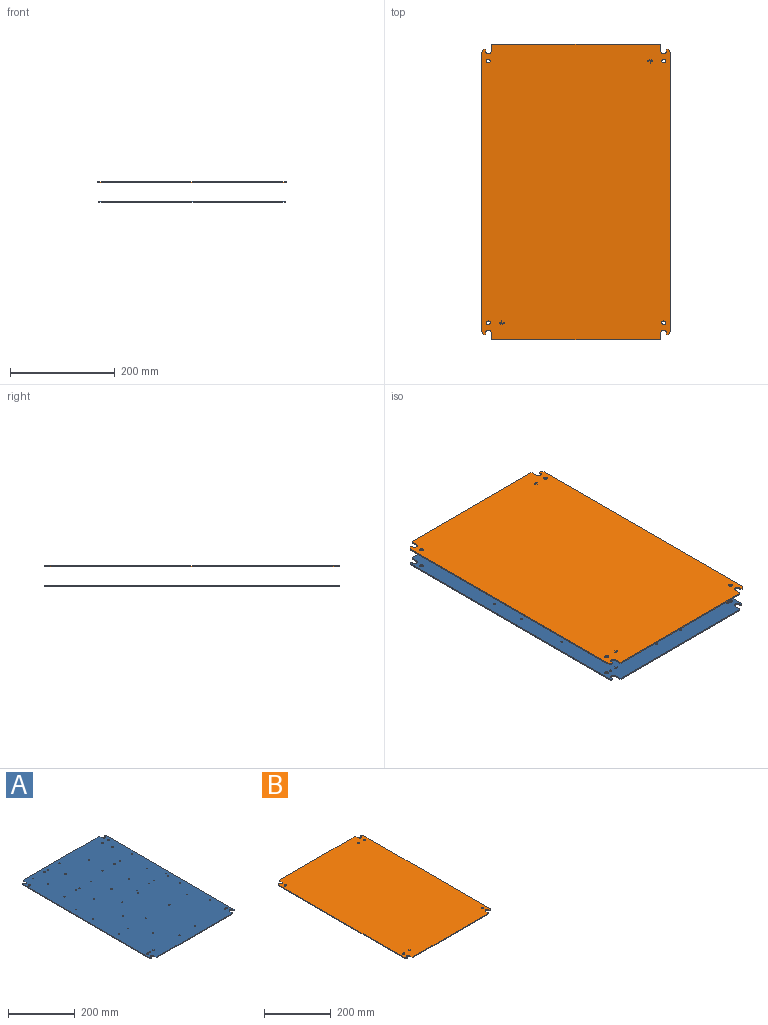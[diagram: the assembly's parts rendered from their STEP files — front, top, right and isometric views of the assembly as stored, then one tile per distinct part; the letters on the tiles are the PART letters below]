
ASSEMBLY  parts=2 mates=1
PART A: 146 faces, bbox 355.3x563.9x2.5 mm
  f0: plane 3.18x0.76mm, normal (0,0,1), area 2.4mm2, adj f6,f7,f8,f9
  f1: plane 9.53x5.13mm, normal (0,0,1), area 10.6mm2, adj f10,f11,f12,f13,f14,f15,f16,f17
  f2: plane 6.35x0.76mm, normal (0,0,1), area 4.8mm2, adj f18,f19,f20,f21
  f3: plane 3.18x0.76mm, normal (0,0,1), area 2.4mm2, adj f22,f23,f24,f25
  f4: plane 6.35x0.76mm, normal (0,0,1), area 4.8mm2, adj f26,f27,f28,f29
  f5: plane 9.53x5.13mm, normal (0,0,1), area 10.6mm2, adj f30,f31,f32,f33,f34,f35,f36,f37
  f6: plane 0.76x0.71mm, normal (1,0,0), area 0.5mm2, adj f0,f7,f9,f38
  f7: plane 3.18x0.71mm, normal (0,-1,0), area 2.3mm2, adj f0,f6,f8,f39
  f8: plane 0.76x0.71mm, normal (-1,0,0), area 0.5mm2, adj f0,f7,f9,f40
  f9: plane 3.18x0.71mm, normal (0,1,0), area 2.3mm2, adj f0,f6,f8,f41
  f10: plane 4.37x0.71mm, normal (1,0,0), area 3.1mm2, adj f1,f11,f17,f42
  f11: plane 0.76x0.71mm, normal (0,-1,0), area 0.5mm2, adj f1,f10,f12,f43
  f12: plane 4.37x0.71mm, normal (-1,0,0), area 3.1mm2, adj f1,f11,f13,f44
  f13: plane 4.38x0.71mm, normal (0,-1,0), area 3.1mm2, adj f1,f12,f14,f45
  f14: plane 0.76x0.71mm, normal (-1,0,0), area 0.5mm2, adj f1,f13,f15,f46
  f15: plane 9.53x0.71mm, normal (0,1,0), area 6.8mm2, adj f1,f14,f16,f47
  f16: plane 0.76x0.71mm, normal (1,0,0), area 0.5mm2, adj f1,f15,f17,f48
  f17: plane 4.38x0.71mm, normal (0,-1,0), area 3.1mm2, adj f1,f10,f16,f49
  f18: plane 0.76x0.71mm, normal (-1,0,0), area 0.5mm2, adj f2,f19,f21,f50
  f19: plane 6.35x0.71mm, normal (0,1,0), area 4.5mm2, adj f2,f18,f20,f51
  f20: plane 0.76x0.71mm, normal (1,0,0), area 0.5mm2, adj f2,f19,f21,f52
  f21: plane 6.35x0.71mm, normal (0,-1,0), area 4.5mm2, adj f2,f18,f20,f53
  f22: plane 0.76x0.71mm, normal (-1,0,0), area 0.5mm2, adj f3,f23,f25,f54
  f23: plane 3.18x0.71mm, normal (0,1,0), area 2.3mm2, adj f3,f22,f24,f55
  f24: plane 0.76x0.71mm, normal (1,0,0), area 0.5mm2, adj f3,f23,f25,f56
  f25: plane 3.18x0.71mm, normal (0,-1,0), area 2.3mm2, adj f3,f22,f24,f57
  f26: plane 0.76x0.71mm, normal (1,0,0), area 0.5mm2, adj f4,f27,f29,f58
  f27: plane 6.35x0.71mm, normal (0,-1,0), area 4.5mm2, adj f4,f26,f28,f59
  f28: plane 0.76x0.71mm, normal (-1,0,0), area 0.5mm2, adj f4,f27,f29,f60
  f29: plane 6.35x0.71mm, normal (0,1,0), area 4.5mm2, adj f4,f26,f28,f61
  f30: plane 4.37x0.71mm, normal (-1,0,0), area 3.1mm2, adj f5,f31,f37,f62
  f31: plane 0.76x0.71mm, normal (0,1,0), area 0.5mm2, adj f5,f30,f32,f63
  f32: plane 4.37x0.71mm, normal (1,0,0), area 3.1mm2, adj f5,f31,f33,f64
  f33: plane 4.38x0.71mm, normal (0,1,0), area 3.1mm2, adj f5,f32,f34,f65
  f34: plane 0.76x0.71mm, normal (1,0,0), area 0.5mm2, adj f5,f33,f35,f66
  f35: plane 9.53x0.71mm, normal (0,-1,0), area 6.8mm2, adj f5,f34,f36,f67
  f36: plane 0.76x0.71mm, normal (-1,0,0), area 0.5mm2, adj f5,f35,f37,f68
  f37: plane 4.38x0.71mm, normal (0,1,0), area 3.1mm2, adj f5,f30,f36,f69
  f38: plane 0.86x0.05mm, normal (0.71,0,0.71), area 0.1mm2, adj f6,f39,f41,f70
  f39: plane 3.28x0.05mm, normal (0,-0.71,0.71), area 0.2mm2, adj f7,f38,f40,f70
  f40: plane 0.86x0.05mm, normal (-0.71,0,0.71), area 0.1mm2, adj f8,f39,f41,f70
  f41: plane 3.28x0.05mm, normal (0,0.71,0.71), area 0.2mm2, adj f9,f38,f40,f70
  f42: plane 4.42x0.05mm, normal (0.71,0,0.71), area 0.3mm2, adj f10,f43,f49,f70
  f43: plane 0.86x0.05mm, normal (0,-0.71,0.71), area 0.1mm2, adj f11,f42,f44,f70
  f44: plane 4.42x0.05mm, normal (-0.71,0,0.71), area 0.3mm2, adj f12,f43,f45,f70
  f45: plane 4.43x0.05mm, normal (0,-0.71,0.71), area 0.3mm2, adj f13,f44,f46,f70
  f46: plane 0.86x0.05mm, normal (-0.71,0,0.71), area 0.1mm2, adj f14,f45,f47,f70
  f47: plane 9.63x0.05mm, normal (0,0.71,0.71), area 0.7mm2, adj f15,f46,f48,f70
  f48: plane 0.86x0.05mm, normal (0.71,0,0.71), area 0.1mm2, adj f16,f47,f49,f70
  f49: plane 4.43x0.05mm, normal (0,-0.71,0.71), area 0.3mm2, adj f17,f42,f48,f70
  f50: plane 0.86x0.05mm, normal (-0.71,0,0.71), area 0.1mm2, adj f18,f51,f53,f70
  f51: plane 6.45x0.05mm, normal (0,0.71,0.71), area 0.5mm2, adj f19,f50,f52,f70
  f52: plane 0.86x0.05mm, normal (0.71,0,0.71), area 0.1mm2, adj f20,f51,f53,f70
  f53: plane 6.45x0.05mm, normal (0,-0.71,0.71), area 0.5mm2, adj f21,f50,f52,f70
  f54: plane 0.86x0.05mm, normal (-0.71,0,0.71), area 0.1mm2, adj f22,f55,f57,f70
  f55: plane 3.28x0.05mm, normal (0,0.71,0.71), area 0.2mm2, adj f23,f54,f56,f70
  f56: plane 0.86x0.05mm, normal (0.71,0,0.71), area 0.1mm2, adj f24,f55,f57,f70
  f57: plane 3.28x0.05mm, normal (0,-0.71,0.71), area 0.2mm2, adj f25,f54,f56,f70
  f58: plane 0.86x0.05mm, normal (0.71,0,0.71), area 0.1mm2, adj f26,f59,f61,f70
  f59: plane 6.45x0.05mm, normal (0,-0.71,0.71), area 0.5mm2, adj f27,f58,f60,f70
  f60: plane 0.86x0.05mm, normal (-0.71,0,0.71), area 0.1mm2, adj f28,f59,f61,f70
  f61: plane 6.45x0.05mm, normal (0,0.71,0.71), area 0.5mm2, adj f29,f58,f60,f70
  f62: plane 4.42x0.05mm, normal (-0.71,0,0.71), area 0.3mm2, adj f30,f63,f69,f70
  f63: plane 0.86x0.05mm, normal (0,0.71,0.71), area 0.1mm2, adj f31,f62,f64,f70
  f64: plane 4.42x0.05mm, normal (0.71,0,0.71), area 0.3mm2, adj f32,f63,f65,f70
  f65: plane 4.43x0.05mm, normal (0,0.71,0.71), area 0.3mm2, adj f33,f64,f66,f70
  f66: plane 0.86x0.05mm, normal (0.71,0,0.71), area 0.1mm2, adj f34,f65,f67,f70
  f67: plane 9.63x0.05mm, normal (0,-0.71,0.71), area 0.7mm2, adj f35,f66,f68,f70
  f68: plane 0.86x0.05mm, normal (-0.71,0,0.71), area 0.1mm2, adj f36,f67,f69,f70
  f69: plane 4.43x0.05mm, normal (0,0.71,0.71), area 0.3mm2, adj f37,f62,f68,f70
  f70: plane 563.88x355.3mm, normal (0,0,1), area 198714.8mm2, adj f38,f39,f40,f41,f42,f43,f44,f45
  f71: cylinder r=5.33mm len=10.67mm, axis (0,0,1), area 41.3mm2, adj f70,f72,f96,f101
  f72: plane 3.51x2.46mm, normal (1,0,0), area 8.6mm2, adj f70,f71,f73,f101
  f73: plane 3.18x2.46mm, normal (0,1,0), area 7.8mm2, adj f70,f72,f74,f101
  f74: plane 2.46x1.91mm, normal (-0.71,0.71,0), area 6.6mm2, adj f70,f73,f101,f145
  f75: plane 2.46x1.91mm, normal (-0.71,-0.71,0), area 6.6mm2, adj f70,f76,f101,f145
  f76: plane 3.18x2.46mm, normal (0,-1,0), area 7.8mm2, adj f70,f75,f77,f101
  f77: plane 3.51x2.46mm, normal (1,0,0), area 8.6mm2, adj f70,f76,f78,f101
  f78: cylinder r=5.33mm len=10.67mm, axis (0,0,1), area 41.3mm2, adj f70,f77,f79,f101
  f79: plane 11.58x2.46mm, normal (-1,0,0), area 28.5mm2, adj f70,f78,f80,f101
  f80: plane 2.46x1.52mm, normal (-0.71,-0.71,0), area 5.3mm2, adj f70,f79,f81,f101
  f81: plane 320.75x2.46mm, normal (0,-1,0), area 790.3mm2, adj f70,f80,f82,f101
  f82: plane 2.46x1.52mm, normal (0.71,-0.71,0), area 5.3mm2, adj f70,f81,f83,f101
  f83: plane 11.58x2.46mm, normal (1,0,0), area 28.5mm2, adj f70,f82,f84,f101
  f84: cylinder r=5.33mm len=10.67mm, axis (0,0,1), area 41.3mm2, adj f70,f83,f85,f101
  f85: plane 3.51x2.46mm, normal (-1,0,0), area 8.6mm2, adj f70,f84,f86,f101
  f86: plane 3.18x2.46mm, normal (0,-1,0), area 7.8mm2, adj f70,f85,f87,f101
  f87: plane 2.46x1.91mm, normal (0.71,-0.71,0), area 6.6mm2, adj f70,f86,f101,f144
  f88: plane 2.46x1.91mm, normal (0.71,0.71,0), area 6.6mm2, adj f70,f89,f101,f144
  f89: plane 3.18x2.46mm, normal (0,1,0), area 7.8mm2, adj f70,f88,f90,f101
  f90: plane 3.51x2.46mm, normal (-1,0,0), area 8.6mm2, adj f70,f89,f91,f101
  f91: cylinder r=5.33mm len=10.67mm, axis (0,0,1), area 41.3mm2, adj f70,f90,f92,f101
  f92: plane 11.58x2.46mm, normal (1,0,0), area 28.5mm2, adj f70,f91,f93,f101
  f93: plane 2.46x1.52mm, normal (0.71,0.71,0), area 5.3mm2, adj f70,f92,f94,f101
  f94: plane 320.75x2.46mm, normal (0,1,0), area 790.3mm2, adj f70,f93,f95,f101
  f95: plane 2.46x1.52mm, normal (-0.71,0.71,0), area 5.3mm2, adj f70,f94,f96,f101
  f96: plane 11.58x2.46mm, normal (-1,0,0), area 28.5mm2, adj f70,f71,f95,f101
  f97: cylinder r=3.57mm len=7.14mm, axis (0,0,1), area 55.2mm2, adj f70,f101
  f98: cylinder r=3.57mm len=7.14mm, axis (0,0,1), area 55.2mm2, adj f70,f101
  f99: cylinder r=3.57mm len=7.14mm, axis (0,0,1), area 55.2mm2, adj f70,f101
  f100: cylinder r=3.57mm len=7.14mm, axis (0,0,1), area 55.2mm2, adj f70,f101
  f101: plane 563.88x355.3mm, normal (0,0,-1), area 198755.8mm2, adj f71,f72,f73,f74,f75,f76,f77,f78
  f102: cylinder r=2.02mm len=4.04mm, axis (0,0,1), area 31.3mm2, adj f70,f101
  f103: cylinder r=2.02mm len=4.04mm, axis (0,0,1), area 31.3mm2, adj f70,f101
  f104: cylinder r=2.02mm len=4.04mm, axis (0,0,1), area 31.3mm2, adj f70,f101
  f105: cylinder r=2.02mm len=4.04mm, axis (0,0,1), area 31.3mm2, adj f70,f101
  f106: cylinder r=2.02mm len=4.04mm, axis (0,0,1), area 31.3mm2, adj f70,f101
  f107: cylinder r=2.02mm len=4.04mm, axis (0,0,1), area 31.3mm2, adj f70,f101
  f108: cylinder r=2.02mm len=4.04mm, axis (0,0,1), area 31.3mm2, adj f70,f101
  f109: cylinder r=2.02mm len=4.04mm, axis (0,0,1), area 31.3mm2, adj f70,f101
  f110: cylinder r=2.02mm len=4.04mm, axis (0,0,1), area 31.3mm2, adj f70,f101
  f111: cylinder r=2.02mm len=4.04mm, axis (0,0,1), area 31.3mm2, adj f70,f101
  f112: cylinder r=2.02mm len=4.04mm, axis (0,0,1), area 31.3mm2, adj f70,f101
  f113: cylinder r=2.02mm len=4.04mm, axis (0,0,1), area 31.3mm2, adj f70,f101
  f114: cylinder r=2.02mm len=4.04mm, axis (0,0,1), area 31.3mm2, adj f70,f101
  f115: cylinder r=2.02mm len=4.04mm, axis (0,0,1), area 31.3mm2, adj f70,f101
  f116: cylinder r=2.02mm len=4.04mm, axis (0,0,1), area 31.3mm2, adj f70,f101
  f117: cylinder r=2.02mm len=4.04mm, axis (0,0,1), area 31.3mm2, adj f70,f101
  f118: cylinder r=2.02mm len=4.04mm, axis (0,0,1), area 31.3mm2, adj f70,f101
  f119: cylinder r=1.73mm len=3.45mm, axis (0,0,1), area 26.7mm2, adj f70,f101
  f120: cylinder r=1.73mm len=3.45mm, axis (0,0,1), area 26.7mm2, adj f70,f101
  f121: cylinder r=1.73mm len=3.45mm, axis (0,0,1), area 26.7mm2, adj f70,f101
  f122: cylinder r=1.73mm len=3.45mm, axis (0,0,1), area 26.7mm2, adj f70,f101
  f123: cylinder r=1.73mm len=3.45mm, axis (0,0,1), area 26.7mm2, adj f70,f101
  f124: cylinder r=1.73mm len=3.45mm, axis (0,0,1), area 26.7mm2, adj f70,f101
  f125: cylinder r=1.73mm len=3.45mm, axis (0,0,1), area 26.7mm2, adj f70,f101
  f126: cylinder r=1.73mm len=3.45mm, axis (0,0,1), area 26.7mm2, adj f70,f101
  f127: cylinder r=1.73mm len=3.45mm, axis (0,0,1), area 26.7mm2, adj f70,f101
  f128: cylinder r=1.73mm len=3.45mm, axis (0,0,1), area 26.7mm2, adj f70,f101
  f129: cylinder r=1.73mm len=3.45mm, axis (0,0,1), area 26.7mm2, adj f70,f101
  f130: cylinder r=1.73mm len=3.45mm, axis (0,0,1), area 26.7mm2, adj f70,f101
  f131: cylinder r=1.73mm len=3.45mm, axis (0,0,1), area 26.7mm2, adj f70,f101
  f132: cylinder r=1.73mm len=3.45mm, axis (0,0,1), area 26.7mm2, adj f70,f101
  f133: cylinder r=1.73mm len=3.45mm, axis (0,0,1), area 26.7mm2, adj f70,f101
  f134: cylinder r=1.73mm len=3.45mm, axis (0,0,1), area 26.7mm2, adj f70,f101
  f135: cylinder r=2.02mm len=4.04mm, axis (0,0,1), area 31.3mm2, adj f70,f101
  f136: cylinder r=2.02mm len=4.04mm, axis (0,0,1), area 31.3mm2, adj f70,f101
  f137: cylinder r=2.02mm len=4.04mm, axis (0,0,1), area 31.3mm2, adj f70,f101
  f138: cylinder r=2.02mm len=4.04mm, axis (0,0,1), area 31.3mm2, adj f70,f101
  f139: cylinder r=2.02mm len=4.04mm, axis (0,0,1), area 31.3mm2, adj f70,f101
  f140: cylinder r=2.02mm len=4.04mm, axis (0,0,1), area 31.3mm2, adj f70,f101
  f141: cylinder r=2.02mm len=4.04mm, axis (0,0,1), area 31.3mm2, adj f70,f101
  f142: cylinder r=2.02mm len=4.04mm, axis (0,0,1), area 31.3mm2, adj f70,f101
  f143: cylinder r=2.02mm len=4.04mm, axis (0,0,1), area 31.3mm2, adj f70,f101
  f144: plane 540.87x2.46mm, normal (1,0,0), area 1332.6mm2, adj f70,f87,f88,f101
  f145: plane 540.87x2.46mm, normal (-1,0,0), area 1332.6mm2, adj f70,f74,f75,f101
PART B: 108 faces, bbox 360.7x563.9x2.5 mm
  f0: cylinder r=3.57mm len=7.14mm, axis (0,0,1), area 55.2mm2, adj f4,f5
  f1: cylinder r=3.57mm len=7.14mm, axis (0,0,1), area 55.2mm2, adj f4,f5
  f2: cylinder r=3.57mm len=7.14mm, axis (0,0,1), area 55.2mm2, adj f4,f5
  f3: cylinder r=3.57mm len=7.14mm, axis (0,0,1), area 55.2mm2, adj f4,f5
  f4: plane 563.88x360.68mm, normal (0,0,1), area 202092.5mm2, adj f0,f1,f2,f3,f6,f7,f8,f9
  f5: plane 563.88x360.68mm, normal (0,0,-1), area 202133.5mm2, adj f0,f1,f2,f3,f6,f7,f8,f9
  f6: plane 320.75x2.46mm, normal (0,-1,0), area 790.3mm2, adj f4,f5,f69,f70
  f7: plane 532.43x2.46mm, normal (1,0,0), area 1311.8mm2, adj f4,f5,f22,f33
  f8: plane 532.43x2.46mm, normal (-1,0,0), area 1311.8mm2, adj f4,f5,f10,f21
  f9: plane 320.75x2.46mm, normal (0,1,0), area 790.3mm2, adj f4,f5,f71,f72
  f10: plane 2.59x2.46mm, normal (-0.92,-0.38,0), area 6.9mm2, adj f4,f5,f8,f11
  f11: plane 3.53x3.53mm, normal (-0.71,-0.71,0), area 12.3mm2, adj f4,f5,f10,f12
  f12: plane 3.18x2.46mm, normal (0,-1,0), area 7.8mm2, adj f4,f5,f11,f13
  f13: plane 3.51x2.46mm, normal (1,0,0), area 8.6mm2, adj f4,f5,f12,f14
  f14: cylinder r=5.33mm len=10.67mm, axis (0,0,1), area 41.3mm2, adj f4,f5,f13,f15
  f15: plane 11.58x2.46mm, normal (-1,0,0), area 28.5mm2, adj f4,f5,f14,f69
  f16: plane 11.58x2.46mm, normal (-1,0,0), area 28.5mm2, adj f4,f5,f17,f72
  f17: cylinder r=5.33mm len=10.67mm, axis (0,0,1), area 41.3mm2, adj f4,f5,f16,f18
  f18: plane 3.51x2.46mm, normal (1,0,0), area 8.6mm2, adj f4,f5,f17,f19
  f19: plane 3.18x2.46mm, normal (0,1,0), area 7.8mm2, adj f4,f5,f18,f20
  f20: plane 3.53x3.53mm, normal (-0.71,0.71,0), area 12.3mm2, adj f4,f5,f19,f21
  f21: plane 2.59x2.46mm, normal (-0.92,0.38,0), area 6.9mm2, adj f4,f5,f8,f20
  f22: plane 2.59x2.46mm, normal (0.92,0.38,0), area 6.9mm2, adj f4,f5,f7,f23
  f23: plane 3.53x3.53mm, normal (0.71,0.71,0), area 12.3mm2, adj f4,f5,f22,f24
  f24: plane 3.18x2.46mm, normal (0,1,0), area 7.8mm2, adj f4,f5,f23,f25
  f25: plane 3.51x2.46mm, normal (-1,0,0), area 8.6mm2, adj f4,f5,f24,f26
  f26: cylinder r=5.33mm len=10.67mm, axis (0,0,1), area 41.3mm2, adj f4,f5,f25,f27
  f27: plane 11.58x2.46mm, normal (1,0,0), area 28.5mm2, adj f4,f5,f26,f71
  f28: plane 11.58x2.46mm, normal (1,0,0), area 28.5mm2, adj f4,f5,f29,f70
  f29: cylinder r=5.33mm len=10.67mm, axis (0,0,1), area 41.3mm2, adj f4,f5,f28,f30
  f30: plane 3.51x2.46mm, normal (-1,0,0), area 8.6mm2, adj f4,f5,f29,f31
  f31: plane 3.18x2.46mm, normal (0,-1,0), area 7.8mm2, adj f4,f5,f30,f32
  f32: plane 3.53x3.53mm, normal (0.71,-0.71,0), area 12.3mm2, adj f4,f5,f31,f33
  f33: plane 2.59x2.46mm, normal (0.92,-0.38,0), area 6.9mm2, adj f4,f5,f7,f32
  f34: plane 6.35x0.76mm, normal (0,0,1), area 4.8mm2, adj f35,f36,f37,f38
  f35: plane 6.35x0.71mm, normal (0,-1,0), area 4.5mm2, adj f34,f36,f37,f42
  f36: plane 0.76x0.71mm, normal (1,0,0), area 0.5mm2, adj f34,f35,f38,f41
  f37: plane 0.76x0.71mm, normal (-1,0,0), area 0.5mm2, adj f34,f35,f38,f40
  f38: plane 6.35x0.71mm, normal (0,1,0), area 4.5mm2, adj f34,f36,f37,f39
  f39: plane 6.45x0.05mm, normal (0,0.71,0.71), area 0.5mm2, adj f4,f38,f40,f41
  f40: plane 0.86x0.05mm, normal (-0.71,0,0.71), area 0.1mm2, adj f4,f37,f39,f42
  f41: plane 0.86x0.05mm, normal (0.71,0,0.71), area 0.1mm2, adj f4,f36,f39,f42
  f42: plane 6.45x0.05mm, normal (0,-0.71,0.71), area 0.5mm2, adj f4,f35,f40,f41
  f43: plane 3.18x0.76mm, normal (0,0,1), area 2.4mm2, adj f44,f45,f46,f47
  f44: plane 3.18x0.71mm, normal (0,-1,0), area 2.3mm2, adj f43,f45,f46,f51
  f45: plane 0.76x0.71mm, normal (1,0,0), area 0.5mm2, adj f43,f44,f47,f50
  f46: plane 0.76x0.71mm, normal (-1,0,0), area 0.5mm2, adj f43,f44,f47,f49
  f47: plane 3.18x0.71mm, normal (0,1,0), area 2.3mm2, adj f43,f45,f46,f48
  f48: plane 3.28x0.05mm, normal (0,0.71,0.71), area 0.2mm2, adj f4,f47,f49,f50
  f49: plane 0.86x0.05mm, normal (-0.71,0,0.71), area 0.1mm2, adj f4,f46,f48,f51
  f50: plane 0.86x0.05mm, normal (0.71,0,0.71), area 0.1mm2, adj f4,f45,f48,f51
  f51: plane 3.28x0.05mm, normal (0,-0.71,0.71), area 0.2mm2, adj f4,f44,f49,f50
  f52: plane 0.76x0.71mm, normal (1,0,0), area 0.5mm2, adj f53,f59,f60,f66
  f53: plane 9.53x0.71mm, normal (0,1,0), area 6.8mm2, adj f52,f54,f60,f68
  f54: plane 0.76x0.71mm, normal (-1,0,0), area 0.5mm2, adj f53,f55,f60,f67
  f55: plane 4.38x0.71mm, normal (0,-1,0), area 3.1mm2, adj f54,f56,f60,f65
  f56: plane 4.37x0.71mm, normal (-1,0,0), area 3.1mm2, adj f55,f57,f60,f63
  f57: plane 0.76x0.71mm, normal (0,-1,0), area 0.5mm2, adj f56,f58,f60,f61
  f58: plane 4.37x0.71mm, normal (1,0,0), area 3.1mm2, adj f57,f59,f60,f62
  f59: plane 4.38x0.71mm, normal (0,-1,0), area 3.1mm2, adj f52,f58,f60,f64
  f60: plane 9.53x5.13mm, normal (0,0,1), area 10.6mm2, adj f52,f53,f54,f55,f56,f57,f58,f59
  f61: plane 0.86x0.05mm, normal (0,-0.71,0.71), area 0.1mm2, adj f4,f57,f62,f63
  f62: plane 4.42x0.05mm, normal (0.71,0,0.71), area 0.3mm2, adj f4,f58,f61,f64
  f63: plane 4.42x0.05mm, normal (-0.71,0,0.71), area 0.3mm2, adj f4,f56,f61,f65
  f64: plane 4.43x0.05mm, normal (0,-0.71,0.71), area 0.3mm2, adj f4,f59,f62,f66
  f65: plane 4.43x0.05mm, normal (0,-0.71,0.71), area 0.3mm2, adj f4,f55,f63,f67
  f66: plane 0.86x0.05mm, normal (0.71,0,0.71), area 0.1mm2, adj f4,f52,f64,f68
  f67: plane 0.86x0.05mm, normal (-0.71,0,0.71), area 0.1mm2, adj f4,f54,f65,f68
  f68: plane 9.63x0.05mm, normal (0,0.71,0.71), area 0.7mm2, adj f4,f53,f66,f67
  f69: plane 2.46x1.52mm, normal (-0.71,-0.71,0), area 5.3mm2, adj f4,f5,f6,f15
  f70: plane 2.46x1.52mm, normal (0.71,-0.71,0), area 5.3mm2, adj f4,f5,f6,f28
  f71: plane 2.46x1.52mm, normal (0.71,0.71,0), area 5.3mm2, adj f4,f5,f9,f27
  f72: plane 2.46x1.52mm, normal (-0.71,0.71,0), area 5.3mm2, adj f4,f5,f9,f16
  f73: plane 6.35x0.76mm, normal (0,0,1), area 4.8mm2, adj f74,f75,f76,f77
  f74: plane 6.35x0.71mm, normal (0,1,0), area 4.5mm2, adj f73,f75,f76,f81
  f75: plane 0.76x0.71mm, normal (-1,0,0), area 0.5mm2, adj f73,f74,f77,f80
  f76: plane 0.76x0.71mm, normal (1,0,0), area 0.5mm2, adj f73,f74,f77,f79
  f77: plane 6.35x0.71mm, normal (0,-1,0), area 4.5mm2, adj f73,f75,f76,f78
  f78: plane 6.45x0.05mm, normal (0,-0.71,0.71), area 0.5mm2, adj f4,f77,f79,f80
  f79: plane 0.86x0.05mm, normal (0.71,0,0.71), area 0.1mm2, adj f4,f76,f78,f81
  f80: plane 0.86x0.05mm, normal (-0.71,0,0.71), area 0.1mm2, adj f4,f75,f78,f81
  f81: plane 6.45x0.05mm, normal (0,0.71,0.71), area 0.5mm2, adj f4,f74,f79,f80
  f82: plane 3.18x0.76mm, normal (0,0,1), area 2.4mm2, adj f83,f84,f85,f86
  f83: plane 3.18x0.71mm, normal (0,1,0), area 2.3mm2, adj f82,f84,f85,f90
  f84: plane 0.76x0.71mm, normal (-1,0,0), area 0.5mm2, adj f82,f83,f86,f89
  f85: plane 0.76x0.71mm, normal (1,0,0), area 0.5mm2, adj f82,f83,f86,f88
  f86: plane 3.18x0.71mm, normal (0,-1,0), area 2.3mm2, adj f82,f84,f85,f87
  f87: plane 3.28x0.05mm, normal (0,-0.71,0.71), area 0.2mm2, adj f4,f86,f88,f89
  f88: plane 0.86x0.05mm, normal (0.71,0,0.71), area 0.1mm2, adj f4,f85,f87,f90
  f89: plane 0.86x0.05mm, normal (-0.71,0,0.71), area 0.1mm2, adj f4,f84,f87,f90
  f90: plane 3.28x0.05mm, normal (0,0.71,0.71), area 0.2mm2, adj f4,f83,f88,f89
  f91: plane 0.76x0.71mm, normal (-1,0,0), area 0.5mm2, adj f92,f98,f99,f105
  f92: plane 9.53x0.71mm, normal (0,-1,0), area 6.8mm2, adj f91,f93,f99,f107
  f93: plane 0.76x0.71mm, normal (1,0,0), area 0.5mm2, adj f92,f94,f99,f106
  f94: plane 4.38x0.71mm, normal (0,1,0), area 3.1mm2, adj f93,f95,f99,f104
  f95: plane 4.37x0.71mm, normal (1,0,0), area 3.1mm2, adj f94,f96,f99,f102
  f96: plane 0.76x0.71mm, normal (0,1,0), area 0.5mm2, adj f95,f97,f99,f100
  f97: plane 4.37x0.71mm, normal (-1,0,0), area 3.1mm2, adj f96,f98,f99,f101
  f98: plane 4.38x0.71mm, normal (0,1,0), area 3.1mm2, adj f91,f97,f99,f103
  f99: plane 9.53x5.13mm, normal (0,0,1), area 10.6mm2, adj f91,f92,f93,f94,f95,f96,f97,f98
  f100: plane 0.86x0.05mm, normal (0,0.71,0.71), area 0.1mm2, adj f4,f96,f101,f102
  f101: plane 4.42x0.05mm, normal (-0.71,0,0.71), area 0.3mm2, adj f4,f97,f100,f103
  f102: plane 4.42x0.05mm, normal (0.71,0,0.71), area 0.3mm2, adj f4,f95,f100,f104
  f103: plane 4.43x0.05mm, normal (0,0.71,0.71), area 0.3mm2, adj f4,f98,f101,f105
  f104: plane 4.43x0.05mm, normal (0,0.71,0.71), area 0.3mm2, adj f4,f94,f102,f106
  f105: plane 0.86x0.05mm, normal (-0.71,0,0.71), area 0.1mm2, adj f4,f91,f103,f107
  f106: plane 0.86x0.05mm, normal (0.71,0,0.71), area 0.1mm2, adj f4,f93,f104,f107
  f107: plane 9.63x0.05mm, normal (0,-0.71,0.71), area 0.7mm2, adj f4,f92,f105,f106
PLACE A t=(0,0,-37.59)mm
PLACE B at identity
MATE cylindrical A.f99 <-> B.f2  axis (0,0,1) through (-167.23,249.78,-35.13)mm
